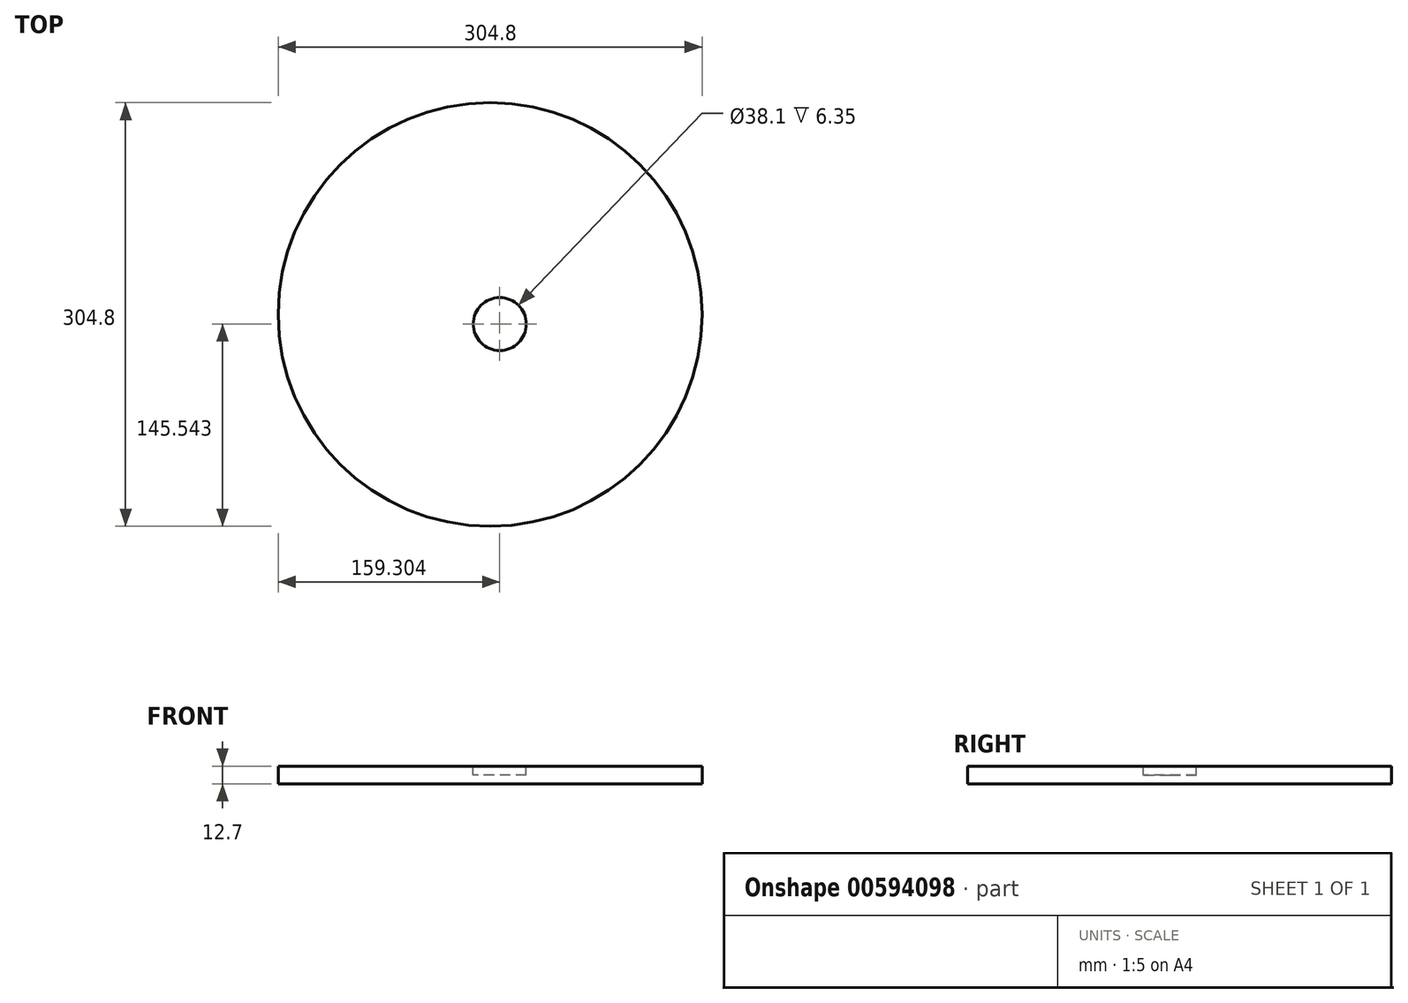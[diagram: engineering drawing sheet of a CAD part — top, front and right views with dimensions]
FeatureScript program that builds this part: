
annotation { "Feature Type Name" : "Feature", "Feature Type Description" : "" }
export const myFeature = defineFeature(function(context is Context, id is Id, definition is map)
    precondition{}
    {
        {
            var Q0;
            Q0=qCreatedBy(makeId("Top.planeOp"),FACE);
            var sketch = newSketch(context, id + "F0", { "sketchPlane" : qUnion([Q0])});
            skCircle(sketch, "E0", {"center": v(0, 0) * mm, "radius": 152.4 * mm});
            skCircle(sketch, "E1", {"center": v(0, 0) * mm, "radius": 16.74 * mm});
            skSolve(sketch);
        }
        {
            var Q0;
            Q0 = qSketchRegion(id + "F0", true);
            var Q1;
            Q1=makeQuery(id+"F0.imprint","IMPRINT",FACE,{"disambiguationData":[TD([[makeQuery(id+"F0.imprint","IMPRINT",EDGE,{"derivedFrom":sQuery(id+"F0.wireOp",EDGE,"E1")}),1.0]])]});
            extrude(context, id + "F1", {"entities" : qUnion([Q0, Q1]), "depth" : 12.7 * mm, "offsetDistance" : 25.4 * mm});
        }
        {
            var Q0;
            Q0=makeQuery(id+"F1.opExtrude","CAP_FACE",FACE,{"disambiguationData":[OSD([sQuery(id+"F0.wireOp",EDGE,"E0")])],"isStart":false});
            var sketch = newSketch(context, id + "F2", { "sketchPlane" : qUnion([Q0])});
            skCircle(sketch, "E2", {"center": v(6.9, -6.86) * mm, "radius": 19.05 * mm});
            skSolve(sketch);
        }
        {
            var Q0;
            Q0=makeQuery(id+"F2.imprint","IMPRINT",FACE,{"disambiguationData":[TD([[makeQuery(id+"F2.imprint","IMPRINT",EDGE,{"derivedFrom":sQuery(id+"F2.wireOp",EDGE,"E2")}),1.0]])]});
            var Q1;
            Q1=sQuery(id+"F2.wireOp",EDGE,"E2");
            extrude(context, id + "F3", {"entities" : qUnion([Q0]), "operationType" : NewBodyOperationType.REMOVE, "surfaceEntities" : qUnion([Q1]), "oppositeDirection" : true, "depth" : 6.35 * mm, "offsetDistance" : 25.4 * mm});
        }
    });
